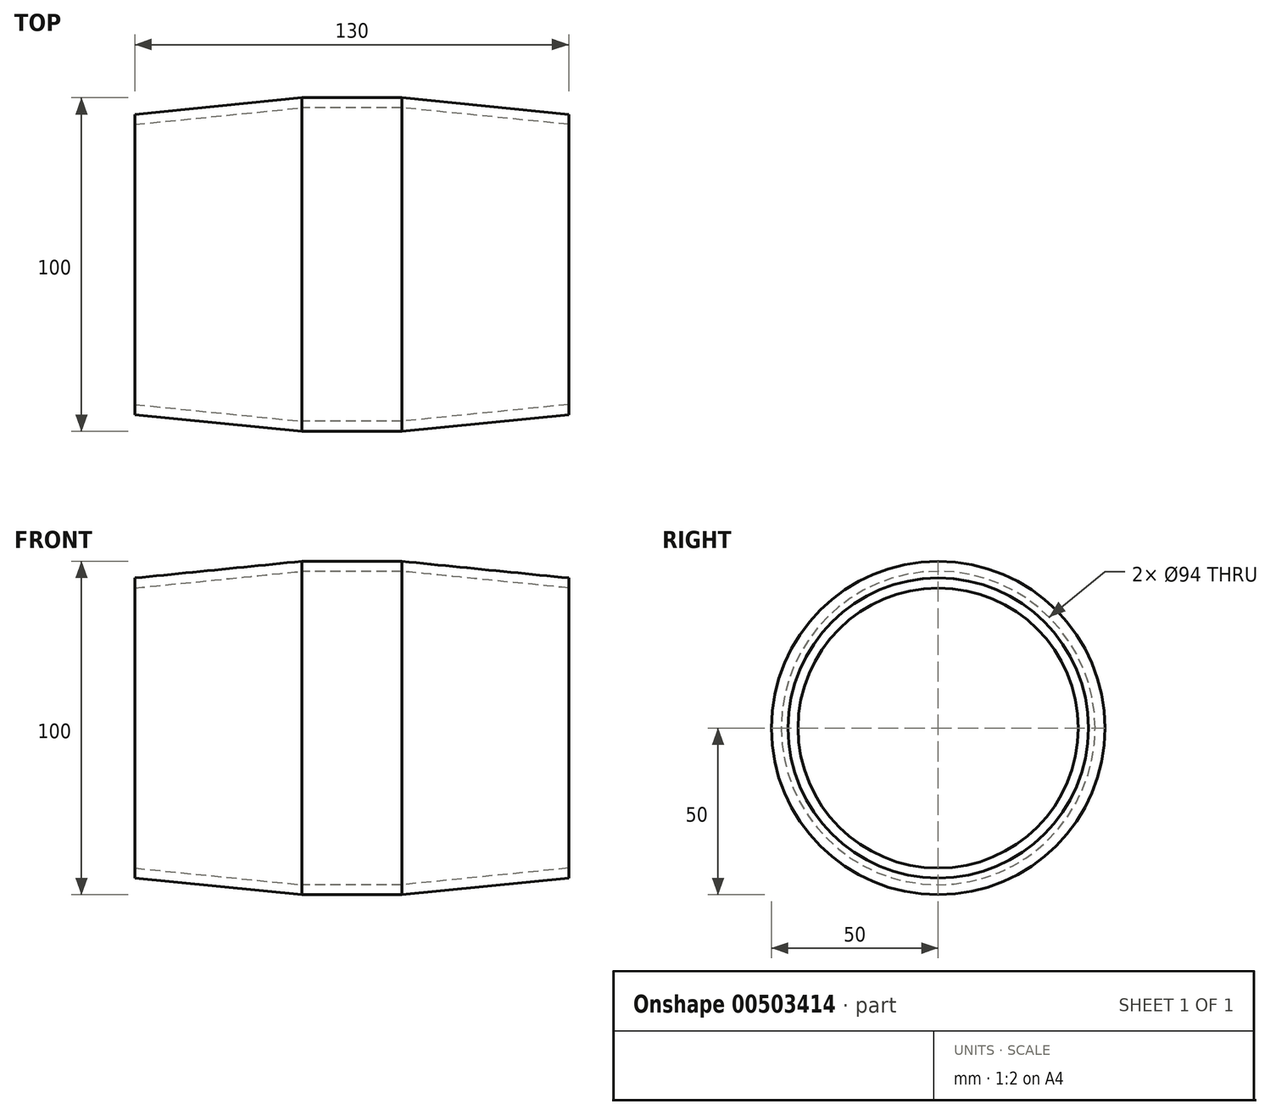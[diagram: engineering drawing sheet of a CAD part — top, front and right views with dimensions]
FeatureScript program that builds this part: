
annotation { "Feature Type Name" : "Feature", "Feature Type Description" : "" }
export const myFeature = defineFeature(function(context is Context, id is Id, definition is map)
    precondition{}
    {
        {
            var Q0;
            Q0=qCreatedBy(makeId("Top.planeOp"),FACE);
            var sketch = newSketch(context, id + "F0", { "sketchPlane" : qUnion([Q0])});
            skLineSegment(sketch, "E0", {"start": v(-15, 50) * mm, "end": v(15, 50) * mm});
            skLineSegment(sketch, "E1.top", {"start": v(-15, 47) * mm, "end": v(15, 47) * mm});
            skLineSegment(sketch, "E2", {"start": v(-65, 45) * mm, "end": v(-65, 42) * mm});
            skLineSegment(sketch, "E3", {"start": v(65, 45) * mm, "end": v(65, 42) * mm});
            skLineSegment(sketch, "E4", {"start": v(-65, 45) * mm, "end": v(-15, 50) * mm});
            skLineSegment(sketch, "E5", {"start": v(-65, 42) * mm, "end": v(-15, 47) * mm});
            skLineSegment(sketch, "E6", {"start": v(15, 47) * mm, "end": v(65, 42) * mm});
            skLineSegment(sketch, "E7", {"start": v(65, 45) * mm, "end": v(15, 50) * mm});
            skSolve(sketch);
        }
        {
            var Q0;
            Q0=qCreatedBy(makeId("Top.planeOp"),FACE);
            var sketch = newSketch(context, id + "F1", { "sketchPlane" : qUnion([Q0])});
            skLineSegment(sketch, "E8", {"start": v(-100, 0) * mm, "end": v(100, 0) * mm});
            skSolve(sketch);
        }
        {
            var Q0;
            Q0=makeQuery(id+"F0.imprint","IMPRINT",FACE,{"disambiguationData":[TD([[makeQuery(id+"F0.imprint","IMPRINT",EDGE,{"derivedFrom":sQuery(id+"F0.wireOp",EDGE,"E0")}),-1.0]])]});
            var Q1;
            Q1=sQuery(id+"F1.wireOp",EDGE,"E8");
            revolve(context, id + "F2", {"entities" : qUnion([Q0]), "axis" : qUnion([Q1]), "revolveType" : RevolveType.FULL});
        }
    });
